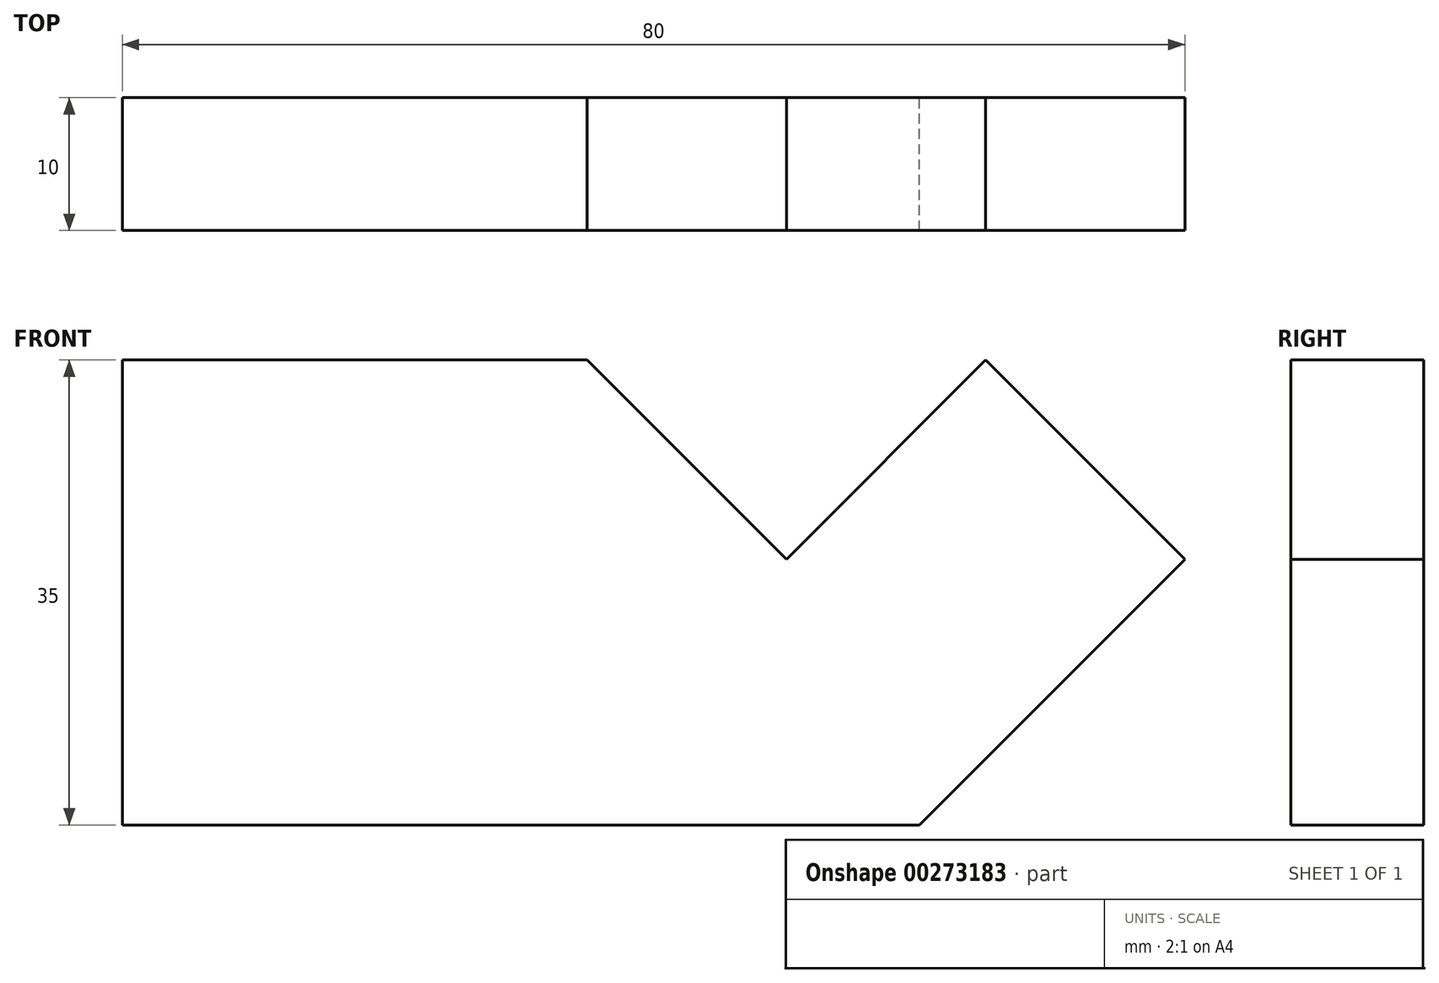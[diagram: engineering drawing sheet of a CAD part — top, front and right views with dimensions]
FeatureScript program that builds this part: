
annotation { "Feature Type Name" : "Feature", "Feature Type Description" : "" }
export const myFeature = defineFeature(function(context is Context, id is Id, definition is map)
    precondition{}
    {
        {
            var Q0;
            Q0=qCreatedBy(makeId("Front.planeOp"),FACE);
            var sketch = newSketch(context, id + "F0", { "sketchPlane" : qUnion([Q0])});
            skLineSegment(sketch, "E0", {"start": v(0, 35) * mm, "end": v(0, 0) * mm});
            skLineSegment(sketch, "E1", {"start": v(35, 35) * mm, "end": v(50, 20) * mm});
            skLineSegment(sketch, "E2", {"start": v(0, 35) * mm, "end": v(35, 35) * mm});
            skLineSegment(sketch, "E3", {"start": v(50, 20) * mm, "end": v(65, 35) * mm});
            skLineSegment(sketch, "E4", {"start": v(65, 35) * mm, "end": v(80, 20) * mm});
            skLineSegment(sketch, "E5", {"start": v(80, 20) * mm, "end": v(60, 0) * mm});
            skLineSegment(sketch, "E6", {"start": v(60, 0) * mm, "end": v(0, 0) * mm});
            skSolve(sketch);
        }
        {
            var Q0;
            Q0 = qSketchRegion(id + "F0", true);
            extrude(context, id + "F1", {"entities" : qUnion([Q0]), "depth" : 10 * mm});
        }
    });
